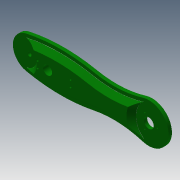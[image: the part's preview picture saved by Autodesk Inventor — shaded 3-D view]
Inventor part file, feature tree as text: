
AUTODESK INVENTOR PART (.ipt)
format: ipt  version: 2013 (Build 170138000, 138)  size: 256,000 bytes
history: native  units: mm
features: sketch x10, extrude x8, chamfer x1
ambient origin geometry x8: Origin, YZ Plane, XZ Plane, XY Plane, X Axis, Y Axis, Z Axis, Center Point
bodies: Solid1 (feature_tree)
feature tree (19):
  extrude  "Extrusion1"  Depth=50.0mm
  extrude  "Extrusion2"  Depth=15.0mm
  extrude  "Extrusion3"  Depth=5.0mm TaperAngle=0.0deg
  extrude  "Extrusion4"  Depth=18.1mm
  extrude  "Extrusion5"  Depth=20.0mm
  extrude  "Extrusion6"  Depth=9.5mm
  sketch  "Sketch7"  dims[d15=9.9mm d16=9.5mm]
  extrude  "Extrusion7"  Depth=9.5mm
  extrude  "Extrusion13"  Depth=3.0mm
  sketch  "Sketch15"  dims[d20=3.0mm d21=3.0mm d22=13.6mm d23=5.0mm d24=0.0mm d26=2.0mm d29=2.0mm d30=2.0mm d31=5.0mm d32=0.0mm d63=5.0mm d64=0.0mm d65=5.0mm d66=0.0mm d72=20.0mm d73=30.0mm d74=7.3mm d75=0.0mm d103=6.0mm d104=5.0mm d105=0.0mm d106=7.0mm d107=2.0mm d108=45.0deg]
  chamfer  "Chamfer2"  Distance=3.0mm
  sketch  "Sketch1"  dims[d0=180.0mm d1=50.0mm]
  sketch  "Sketch2"  dims[d2=5.0mm d3=0.0mm d4=15.0mm]
  sketch  "Sketch3"  dims[d5=15.0mm d6=5.0mm d7=0.0mm]
  sketch  "Sketch4"  dims[d9=34.65mm d10=18.1mm]
  sketch  "Sketch5"  dims[d11=55.0mm d12=20.0mm]
  sketch  "Sketch6"  dims[d13=40.2mm d14=9.5mm]
  sketch  "Sketch8"  dims[d17=9.9mm d18=3.0mm]
  sketch  "Sketch14"  dims[d19=3.0mm]
